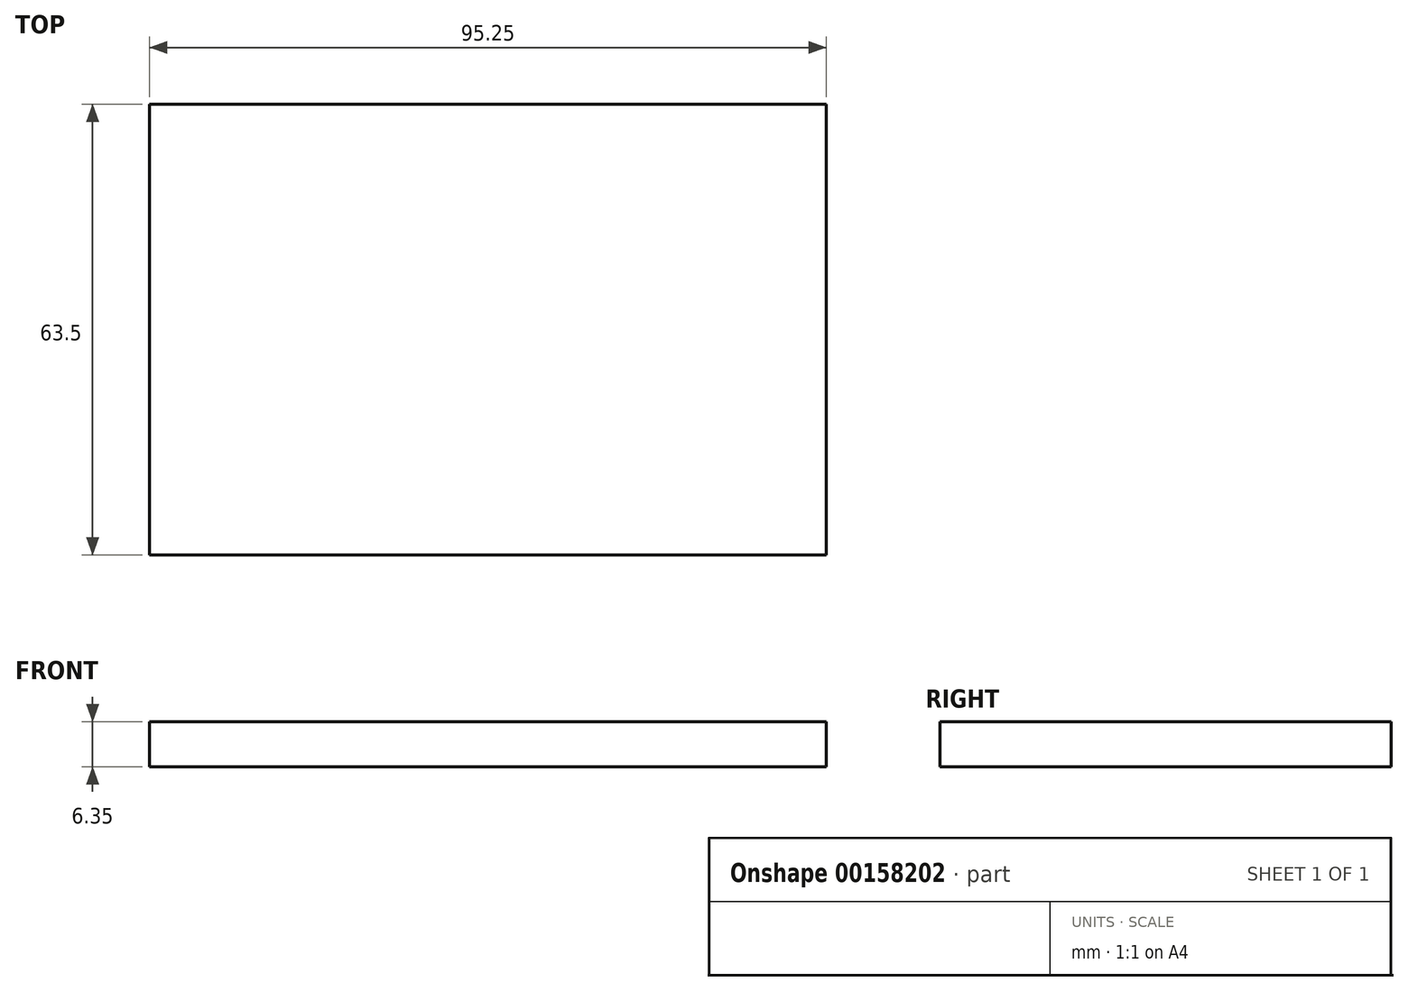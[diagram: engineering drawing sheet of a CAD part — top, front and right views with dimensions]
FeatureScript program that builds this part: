
annotation { "Feature Type Name" : "Feature", "Feature Type Description" : "" }
export const myFeature = defineFeature(function(context is Context, id is Id, definition is map)
    precondition{}
    {
        {
            var Q0;
            Q0=qCreatedBy(makeId("Top.planeOp"),FACE);
            var sketch = newSketch(context, id + "F0", { "sketchPlane" : qUnion([Q0])});
            skLineSegment(sketch, "E0.bottom", {"start": v(-43.3, -35.57) * mm, "end": v(51.95, -35.57) * mm});
            skLineSegment(sketch, "E0.top", {"start": v(-43.3, 27.93) * mm, "end": v(51.95, 27.93) * mm});
            skLineSegment(sketch, "E0.left", {"start": v(-43.3, -35.57) * mm, "end": v(-43.3, 27.93) * mm});
            skLineSegment(sketch, "E0.right", {"start": v(51.95, -35.57) * mm, "end": v(51.95, 27.93) * mm});
            skSolve(sketch);
        }
        {
            var Q0;
            Q0 = qSketchRegion(id + "F0", true);
            extrude(context, id + "F1", {"entities" : qUnion([Q0]), "oppositeDirection" : true, "depth" : 6.35 * mm});
        }
    });
